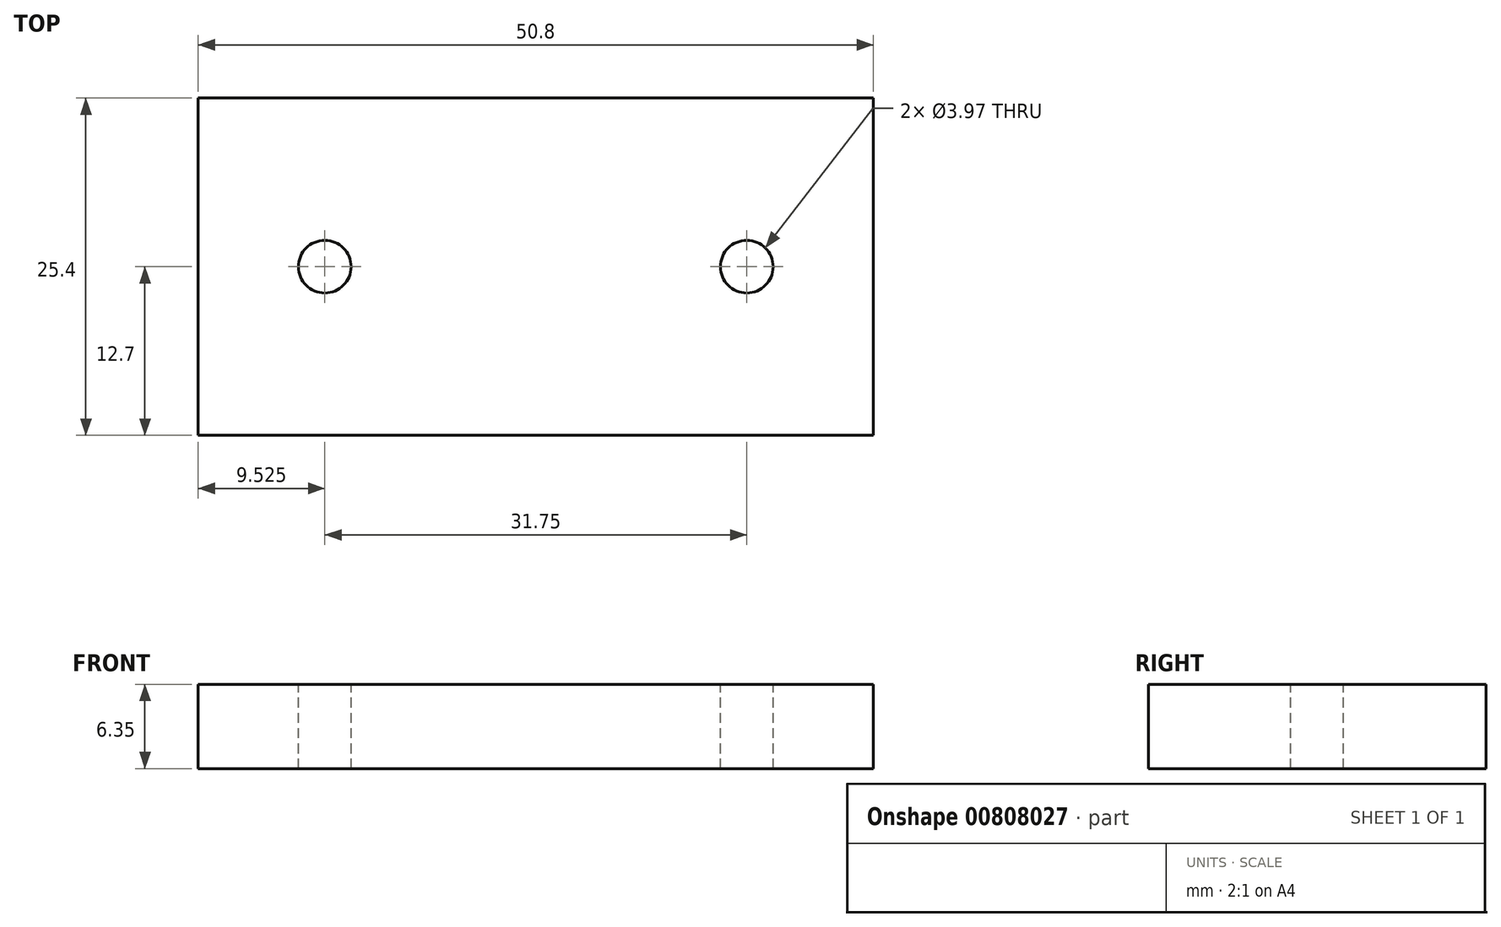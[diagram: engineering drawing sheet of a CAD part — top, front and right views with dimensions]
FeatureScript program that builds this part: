
annotation { "Feature Type Name" : "Feature", "Feature Type Description" : "" }
export const myFeature = defineFeature(function(context is Context, id is Id, definition is map)
    precondition{}
    {
        {
            var Q0;
            Q0=qCreatedBy(makeId("Top.planeOp"),FACE);
            var sketch = newSketch(context, id + "F0", { "sketchPlane" : qUnion([Q0])});
            skLineSegment(sketch, "E0.bottom", {"start": v(25.4, -12.7) * mm, "end": v(-25.4, -12.7) * mm});
            skLineSegment(sketch, "E0.top", {"start": v(25.4, 12.7) * mm, "end": v(-25.4, 12.7) * mm});
            skLineSegment(sketch, "E0.left", {"start": v(25.4, -12.7) * mm, "end": v(25.4, 12.7) * mm});
            skLineSegment(sketch, "E0.right", {"start": v(-25.4, -12.7) * mm, "end": v(-25.4, 12.7) * mm});
            skPoint(sketch, "E0.middle", {"position": v(0, 0) * mm});
            skSolve(sketch);
        }
        {
            var Q0;
            Q0 = qSketchRegion(id + "F0", true);
            extrude(context, id + "F1", {"entities" : qUnion([Q0]), "oppositeDirection" : true, "depth" : 6.35 * mm, "offsetDistance" : 25.4 * mm});
        }
        {
            var Q0;
            Q0=makeQuery(id+"F1.opExtrude","CAP_FACE",FACE,{"disambiguationData":[OSD([sQuery(id+"F0.wireOp",EDGE,"E0.bottom"),sQuery(id+"F0.wireOp",EDGE,"E0.top"),sQuery(id+"F0.wireOp",EDGE,"E0.left"),sQuery(id+"F0.wireOp",EDGE,"E0.right")])],"isStart":true});
            var sketch = newSketch(context, id + "F2", { "sketchPlane" : qUnion([Q0])});
            skCircle(sketch, "E1", {"center": v(-15.88, 0) * mm, "radius": 1.98 * mm});
            skCircle(sketch, "E2", {"center": v(15.88, 0) * mm, "radius": 1.98 * mm});
            skSolve(sketch);
        }
        {
            var Q0;
            Q0 = qSketchRegion(id + "F2", true);
            extrude(context, id + "F3", {"entities" : qUnion([Q0]), "operationType" : NewBodyOperationType.REMOVE, "endBound" : BoundingType.THROUGH_ALL, "oppositeDirection" : true, "depth" : 25.4 * mm, "offsetDistance" : 25.4 * mm});
        }
    });
